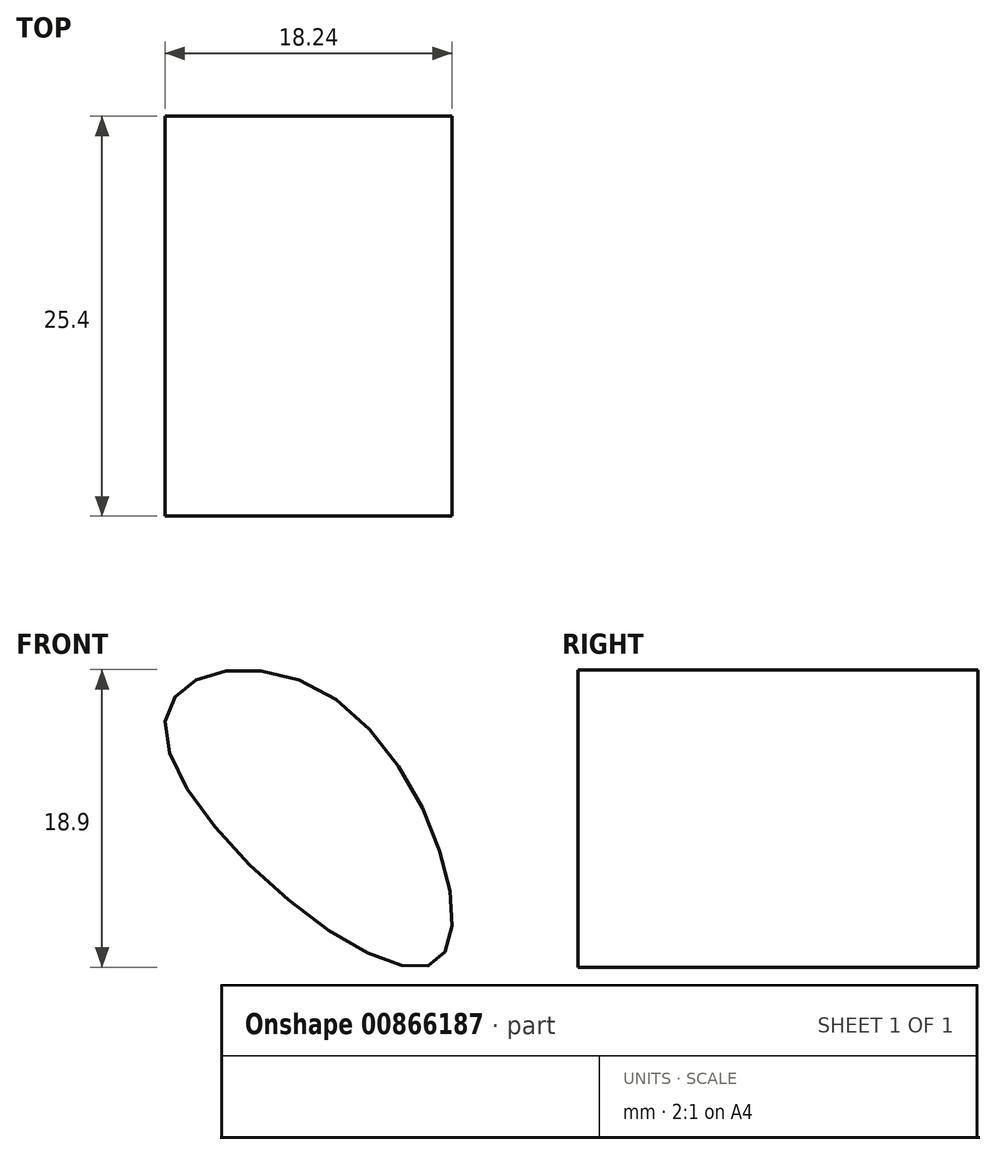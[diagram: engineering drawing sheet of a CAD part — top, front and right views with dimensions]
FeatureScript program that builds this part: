
annotation { "Feature Type Name" : "Feature", "Feature Type Description" : "" }
export const myFeature = defineFeature(function(context is Context, id is Id, definition is map)
    precondition{}
    {
        {
            var Q0;
            Q0=qCreatedBy(makeId("Front.planeOp"),FACE);
            var sketch = newSketch(context, id + "F0", { "sketchPlane" : qUnion([Q0])});
            skFitSpline(sketch, "E0", {"points": [v(0, 36.73) * mm, v(-10.86, 34.96) * mm, v(5.98, 19.87) * mm, v(0, 36.73) * mm]});
            skSolve(sketch);
        }
        {
            var Q0;
            Q0 = qSketchRegion(id + "F0", true);
            extrude(context, id + "F1", {"entities" : qUnion([Q0]), "depth" : 25.4 * mm, "offsetDistance" : 25.4 * mm});
        }
    });
